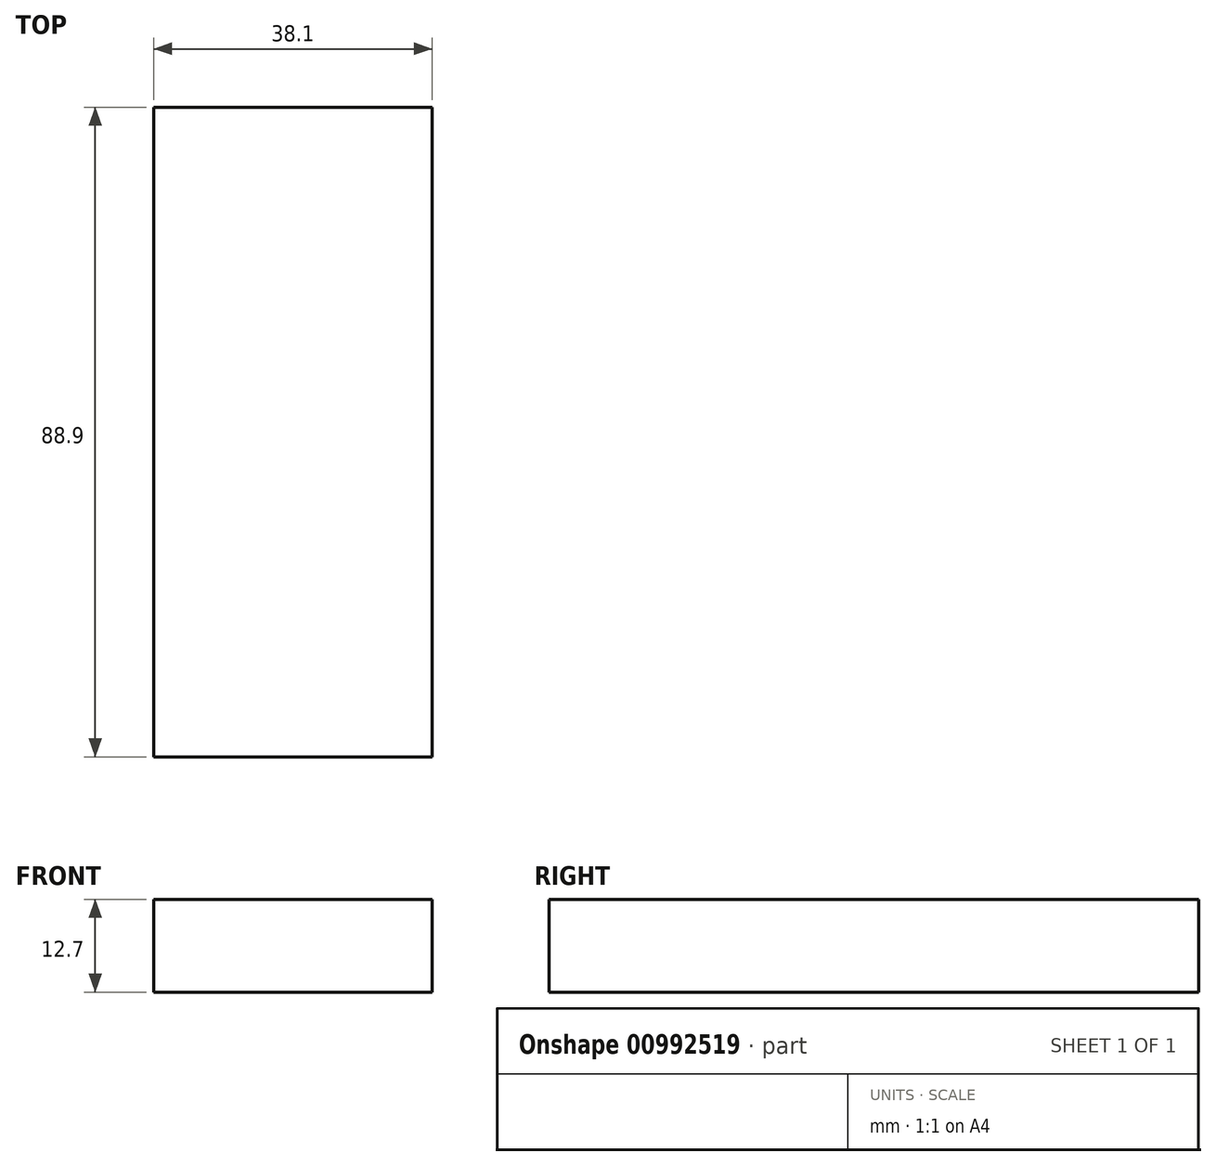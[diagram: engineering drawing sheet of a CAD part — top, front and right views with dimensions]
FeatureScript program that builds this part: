
annotation { "Feature Type Name" : "Feature", "Feature Type Description" : "" }
export const myFeature = defineFeature(function(context is Context, id is Id, definition is map)
    precondition{}
    {
        {
            var Q0;
            Q0=qCreatedBy(makeId("Top.planeOp"),FACE);
            var sketch = newSketch(context, id + "F0", { "sketchPlane" : qUnion([Q0])});
            skLineSegment(sketch, "E0.bottom", {"start": v(-19.05, 44.45) * mm, "end": v(19.05, 44.45) * mm});
            skLineSegment(sketch, "E0.top", {"start": v(-19.05, -44.45) * mm, "end": v(19.05, -44.45) * mm});
            skLineSegment(sketch, "E0.left", {"start": v(-19.05, 44.45) * mm, "end": v(-19.05, -44.45) * mm});
            skLineSegment(sketch, "E0.right", {"start": v(19.05, 44.45) * mm, "end": v(19.05, -44.45) * mm});
            skPoint(sketch, "E0.middle", {"position": v(0, 0) * mm});
            skSolve(sketch);
        }
        {
            var Q0;
            Q0=makeQuery(id+"F0.imprint","IMPRINT",FACE,{"disambiguationData":[TD([[makeQuery(id+"F0.imprint","IMPRINT",EDGE,{"derivedFrom":sQuery(id+"F0.wireOp",EDGE,"E0.bottom")}),-1.0]])]});
            extrude(context, id + "F1", {"entities" : qUnion([Q0]), "endBound" : BoundingType.SYMMETRIC, "depth" : 12.7 * mm, "offsetDistance" : 25.4 * mm});
        }
    });
